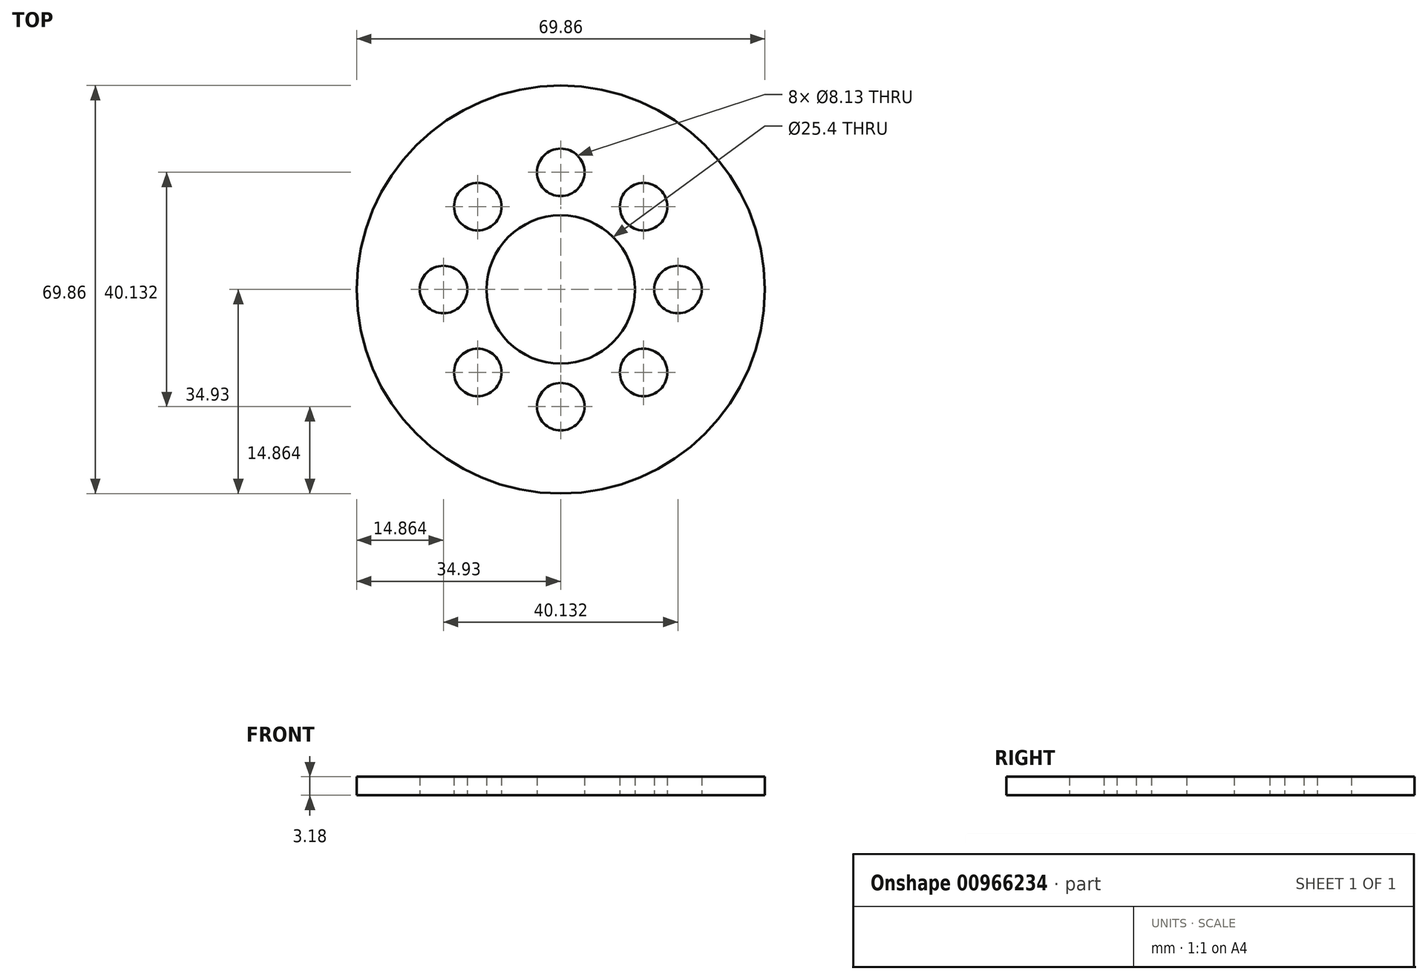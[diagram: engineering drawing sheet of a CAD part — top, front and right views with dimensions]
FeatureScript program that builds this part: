
annotation { "Feature Type Name" : "Feature", "Feature Type Description" : "" }
export const myFeature = defineFeature(function(context is Context, id is Id, definition is map)
    precondition{}
    {
        {
            var Q0;
            Q0=qCreatedBy(makeId("Top.planeOp"),FACE);
            var sketch = newSketch(context, id + "F0", { "sketchPlane" : qUnion([Q0])});
            skCircle(sketch, "E0", {"center": v(0, 0) * mm, "radius": 34.93 * mm});
            skCircle(sketch, "E1", {"center": v(0, 0) * mm, "radius": 12.7 * mm});
            skCircle(sketch, "E2", {"center": v(0, 20.07) * mm, "radius": 4.06 * mm});
            skCircle(sketch, "E3.1.0", {"center": v(-14.19, 14.19) * mm, "radius": 4.06 * mm});
            skCircle(sketch, "E3.2.0", {"center": v(-20.07, 0) * mm, "radius": 4.06 * mm});
            skCircle(sketch, "E3.3.0", {"center": v(-14.19, -14.19) * mm, "radius": 4.06 * mm});
            skCircle(sketch, "E3.4.0", {"center": v(0, -20.07) * mm, "radius": 4.06 * mm});
            skCircle(sketch, "E3.5.0", {"center": v(14.19, -14.19) * mm, "radius": 4.06 * mm});
            skCircle(sketch, "E3.6.0", {"center": v(20.07, 0) * mm, "radius": 4.06 * mm});
            skCircle(sketch, "E3.7.0", {"center": v(14.19, 14.19) * mm, "radius": 4.06 * mm});
            skSolve(sketch);
        }
        {
            var Q0;
            Q0=makeQuery(id+"F0.imprint","IMPRINT",FACE,{"disambiguationData":[TD([[makeQuery(id+"F0.imprint","IMPRINT",EDGE,{"derivedFrom":sQuery(id+"F0.wireOp",EDGE,"E0")}),1.0]])]});
            extrude(context, id + "F1", {"entities" : qUnion([Q0]), "depth" : 3.17 * mm});
        }
    });
